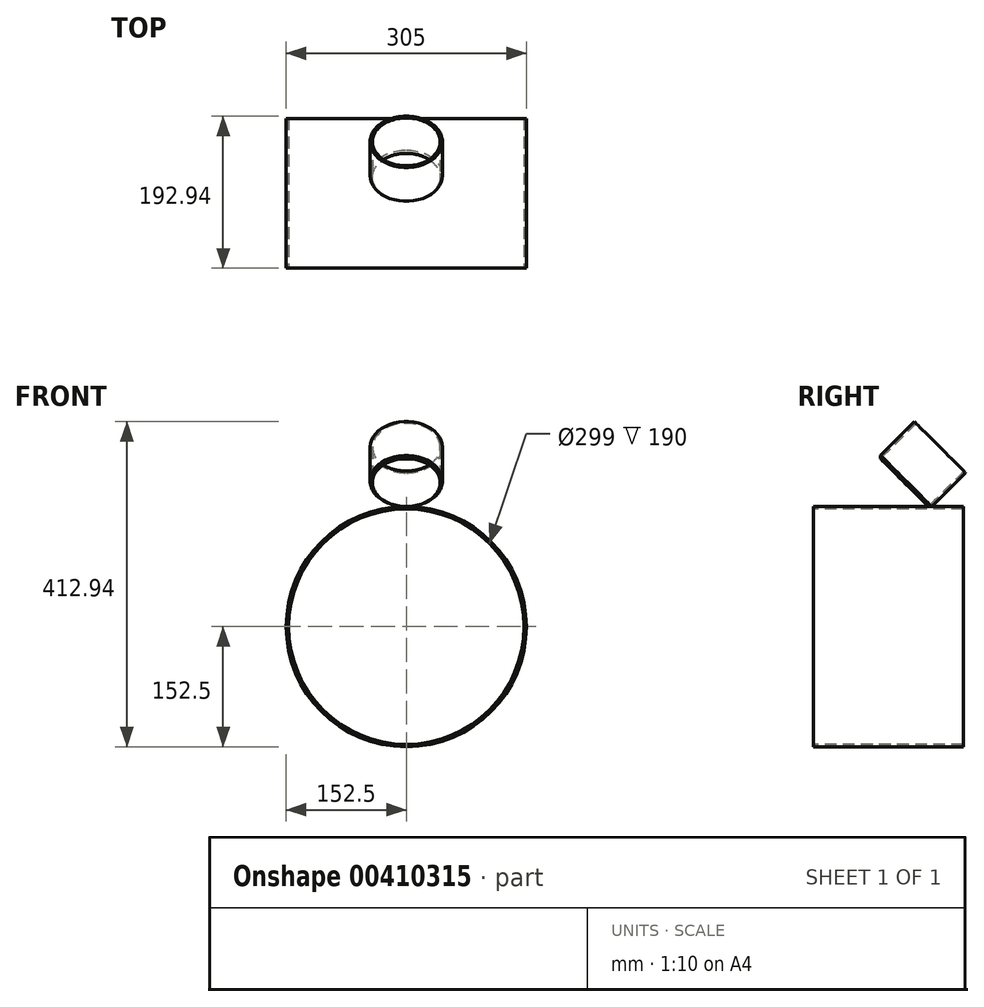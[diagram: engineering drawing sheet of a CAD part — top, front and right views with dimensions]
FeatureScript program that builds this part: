
annotation { "Feature Type Name" : "Feature", "Feature Type Description" : "" }
export const myFeature = defineFeature(function(context is Context, id is Id, definition is map)
    precondition{}
    {
        {
            var Q0;
            Q0=qCreatedBy(makeId("Right.planeOp"),FACE);
            var sketch = newSketch(context, id + "F0", { "sketchPlane" : qUnion([Q0])});
            skLineSegment(sketch, "E0", {"start": v(0, 0) * mm, "end": v(626.56, 0) * mm, "construction": true});
            skLineSegment(sketch, "E1", {"start": v(0, 149.5) * mm, "end": v(190, 149.5) * mm});
            skLineSegment(sketch, "E2", {"start": v(0, 149.5) * mm, "end": v(0, 152.5) * mm});
            skLineSegment(sketch, "E3", {"start": v(0, 152.5) * mm, "end": v(190, 152.5) * mm});
            skLineSegment(sketch, "E4", {"start": v(190, 152.5) * mm, "end": v(190, 149.5) * mm});
            skSolve(sketch);
        }
        {
            var Q0;
            Q0 = qSketchRegion(id + "F0", true);
            var Q1;
            Q1=sQuery(id+"F0.wireOp",EDGE,"E0");
            revolve(context, id + "F1", {"entities" : qUnion([Q0]), "axis" : qUnion([Q1]), "revolveType" : RevolveType.FULL});
        }
        {
            var Q0;
            Q0=qCreatedBy(makeId("Right.planeOp"),FACE);
            var sketch = newSketch(context, id + "F2", { "sketchPlane" : qUnion([Q0])});
            skLineSegment(sketch, "E5", {"start": v(0, 0) * mm, "end": v(85, 0) * mm, "construction": true});
            skLineSegment(sketch, "E6", {"start": v(85, 0) * mm, "end": v(85, 152.5) * mm, "construction": true});
            skLineSegment(sketch, "E7", {"start": v(85, 152.5) * mm, "end": v(137.94, 205.44) * mm, "construction": true});
            skLineSegment(sketch, "E8.0", {"start": v(145.81, 152.5) * mm, "end": v(190.82, 197.5) * mm});
            skLineSegment(sketch, "E9.0", {"start": v(150.05, 152.5) * mm, "end": v(192.94, 195.39) * mm});
            skLineSegment(sketch, "E10", {"start": v(85, 152.5) * mm, "end": v(150.05, 152.5) * mm, "construction": true});
            skLineSegment(sketch, "E11", {"start": v(190.82, 197.5) * mm, "end": v(192.94, 195.39) * mm});
            skLineSegment(sketch, "E12", {"start": v(145.81, 152.5) * mm, "end": v(150.05, 152.5) * mm});
            skSolve(sketch);
        }
        {
            var Q0;
            Q0 = qSketchRegion(id + "F2", true);
            var Q1;
            Q1=sQuery(id+"F2.wireOp",EDGE,"E7");
            revolve(context, id + "F3", {"operationType" : NewBodyOperationType.ADD, "entities" : qUnion([Q0]), "axis" : qUnion([Q1]), "revolveType" : RevolveType.FULL});
        }
    });
